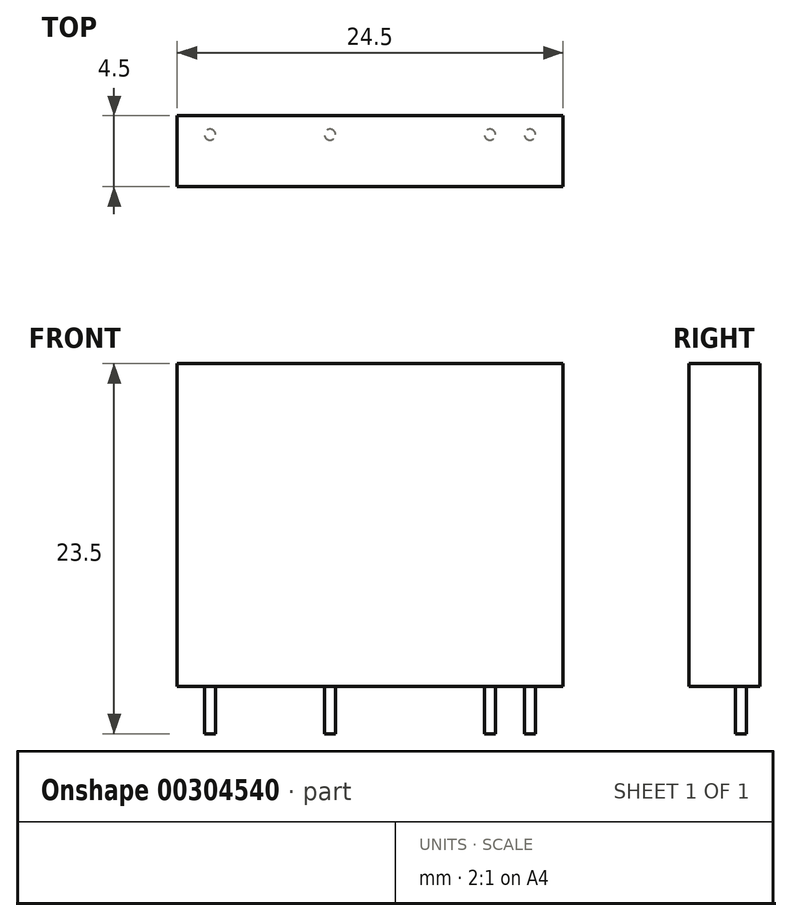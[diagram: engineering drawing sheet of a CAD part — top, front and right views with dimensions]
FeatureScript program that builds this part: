
annotation { "Feature Type Name" : "Feature", "Feature Type Description" : "" }
export const myFeature = defineFeature(function(context is Context, id is Id, definition is map)
    precondition{}
    {
        {
            var Q0;
            Q0=qCreatedBy(makeId("Top.planeOp"),FACE);
            var sketch = newSketch(context, id + "F0", { "sketchPlane" : qUnion([Q0])});
            skLineSegment(sketch, "E0.bottom", {"start": v(12.25, 2.25) * mm, "end": v(-12.25, 2.25) * mm});
            skLineSegment(sketch, "E0.top", {"start": v(12.25, -2.25) * mm, "end": v(-12.25, -2.25) * mm});
            skLineSegment(sketch, "E0.left", {"start": v(12.25, 2.25) * mm, "end": v(12.25, -2.25) * mm});
            skLineSegment(sketch, "E0.right", {"start": v(-12.25, 2.25) * mm, "end": v(-12.25, -2.25) * mm});
            skPoint(sketch, "E0.middle", {"position": v(0, 0) * mm});
            skSolve(sketch);
        }
        {
            var Q0;
            Q0 = qSketchRegion(id + "F0", true);
            extrude(context, id + "F1", {"entities" : qUnion([Q0]), "depth" : 20.5 * mm});
        }
        {
            var Q0;
            Q0=qCreatedBy(makeId("Top.planeOp"),FACE);
            var sketch = newSketch(context, id + "F2", { "sketchPlane" : qUnion([Q0])});
            skLineSegment(sketch, "E1", {"start": v(-10.17, 1.05) * mm, "end": v(10.15, 1.05) * mm, "construction": true});
            skCircle(sketch, "E2", {"center": v(-10.17, 1.05) * mm, "radius": 0.35 * mm});
            skCircle(sketch, "E3", {"center": v(-2.55, 1.05) * mm, "radius": 0.35 * mm});
            skCircle(sketch, "E4", {"center": v(7.61, 1.05) * mm, "radius": 0.35 * mm});
            skCircle(sketch, "E5", {"center": v(10.15, 1.05) * mm, "radius": 0.35 * mm});
            skSolve(sketch);
        }
        {
            var Q0;
            Q0 = qSketchRegion(id + "F2", true);
            extrude(context, id + "F3", {"entities" : qUnion([Q0]), "operationType" : NewBodyOperationType.ADD, "oppositeDirection" : true, "depth" : 3 * mm});
        }
    });
